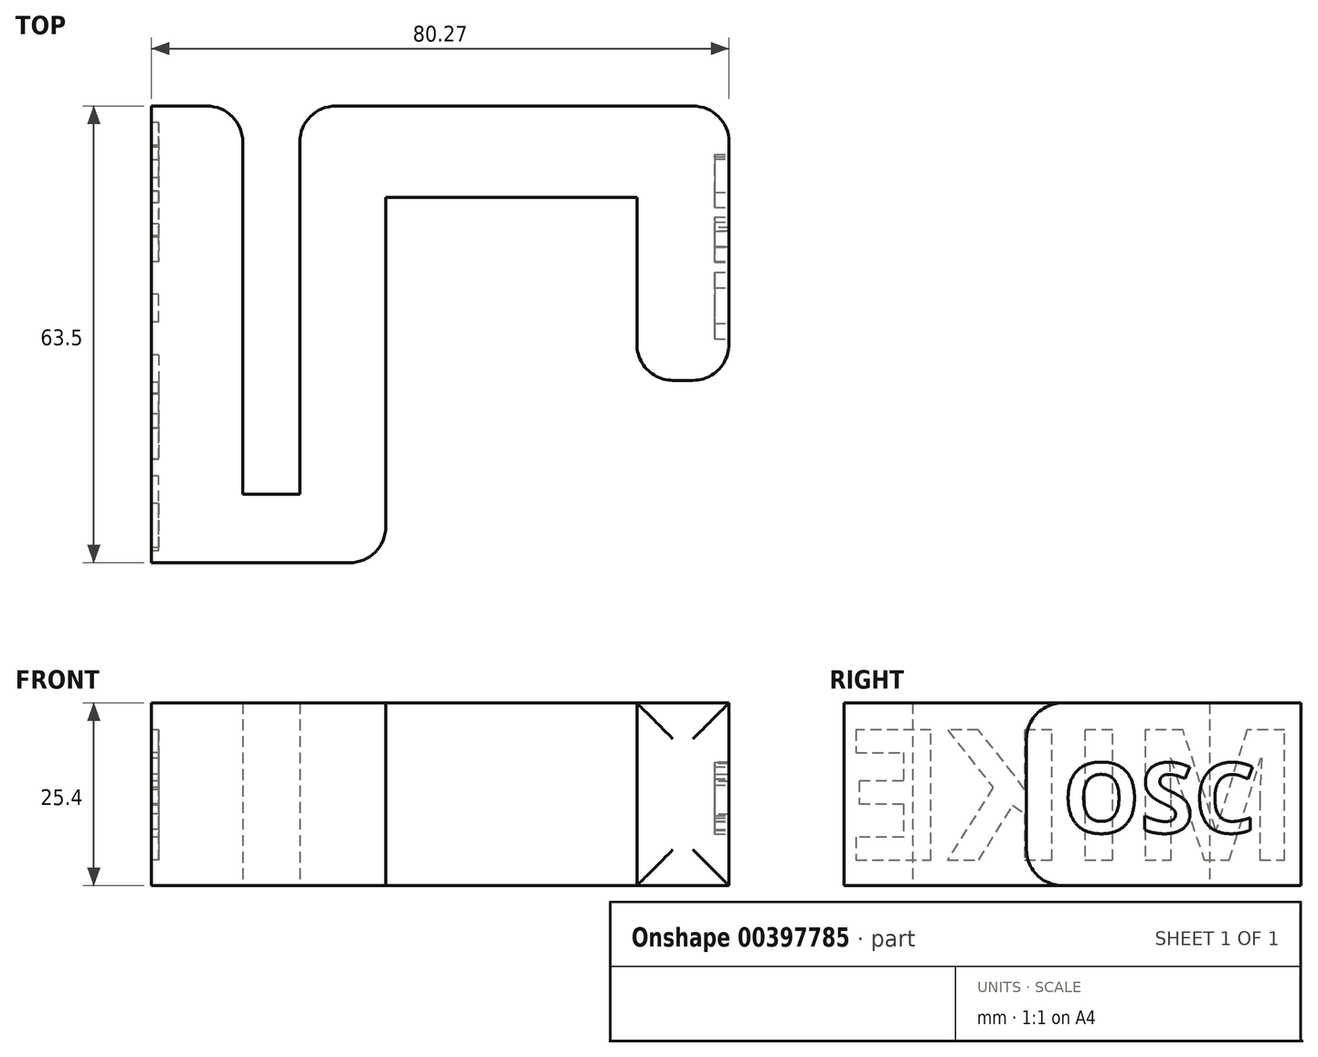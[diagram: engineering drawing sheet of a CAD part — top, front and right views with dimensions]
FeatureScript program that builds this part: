
annotation { "Feature Type Name" : "Feature", "Feature Type Description" : "" }
export const myFeature = defineFeature(function(context is Context, id is Id, definition is map)
    precondition{}
    {
        {
            var Q0;
            Q0=qCreatedBy(makeId("Top.planeOp"),FACE);
            var sketch = newSketch(context, id + "F0", { "sketchPlane" : qUnion([Q0])});
            skLineSegment(sketch, "E0", {"start": v(0, 0) * mm, "end": v(0, 63.5) * mm});
            skLineSegment(sketch, "E1", {"start": v(0, 63.5) * mm, "end": v(12.7, 63.5) * mm});
            skLineSegment(sketch, "E2", {"start": v(12.7, 63.5) * mm, "end": v(12.7, 9.53) * mm});
            skLineSegment(sketch, "E3", {"start": v(12.7, 9.53) * mm, "end": v(20.64, 9.53) * mm});
            skLineSegment(sketch, "E4", {"start": v(20.64, 9.53) * mm, "end": v(20.64, 63.5) * mm});
            skLineSegment(sketch, "E5", {"start": v(20.64, 63.5) * mm, "end": v(80.27, 63.5) * mm});
            skLineSegment(sketch, "E6", {"start": v(80.27, 63.5) * mm, "end": v(80.27, 25.35) * mm});
            skLineSegment(sketch, "E7", {"start": v(80.27, 25.35) * mm, "end": v(67.48, 25.35) * mm});
            skLineSegment(sketch, "E8", {"start": v(67.48, 25.35) * mm, "end": v(67.48, 50.8) * mm});
            skLineSegment(sketch, "E9", {"start": v(67.48, 50.8) * mm, "end": v(32.58, 50.8) * mm});
            skLineSegment(sketch, "E10", {"start": v(32.58, 50.8) * mm, "end": v(32.58, 0) * mm});
            skLineSegment(sketch, "E11", {"start": v(32.58, 0) * mm, "end": v(0, 0) * mm});
            skSolve(sketch);
        }
        {
            var Q0;
            Q0=makeQuery(id+"F0.imprint","IMPRINT",FACE,{"disambiguationData":[TD([[makeQuery(id+"F0.imprint","IMPRINT",EDGE,{"derivedFrom":sQuery(id+"F0.wireOp",EDGE,"E0")}),-1.0]])]});
            extrude(context, id + "F1", {"entities" : qUnion([Q0]), "depth" : 25.4 * mm});
        }
        {
            var Q0;
            Q0=makeQuery(id+"F1.opExtrude","SWEPT_FACE",FACE,{"disambiguationData":[OSD([sQuery(id+"F0.wireOp",EDGE,"E0")])]});
            var sketch = newSketch(context, id + "F2", { "sketchPlane" : qUnion([Q0])});
            skText(sketch, "E12", { "text": "MIKE", "fontName": "OpenSans-Bold.ttf"});
            const initialGuessF2  = {"E12": [-0.0635, 0.00354, 1, 0, 0.01826]};
            skSetInitialGuess(sketch, initialGuessF2);
            skSolve(sketch);
        }
        {
            var Q0;
            Q0=qSketchRegion(id+"F2",true);
            extrude(context, id + "F3", {"entities" : qUnion([Q0]), "operationType" : NewBodyOperationType.REMOVE, "oppositeDirection" : true, "depth" : 1 * mm});
        }
        {
            var Q0;
            Q0=makeQuery(id+"F1.opExtrude","CAP_EDGE",EDGE,{"disambiguationData":[OSD([sQuery(id+"F0.wireOp",EDGE,"E7")])],"isStart":false});
            var Q1;
            Q1=makeQuery(id+"F1.opExtrude","CAP_EDGE",EDGE,{"disambiguationData":[OSD([sQuery(id+"F0.wireOp",EDGE,"E7")])],"isStart":true});
            var Q2;
            Q2=makeQuery(id+"F1.opExtrude","SWEPT_EDGE",EDGE,{"disambiguationData":[OSD([sQuery(id+"F0.wireOp",EDGE,"E6"),sQuery(id+"F0.wireOp",EDGE,"E7")])]});
            var Q3;
            Q3=makeQuery(id+"F1.opExtrude","SWEPT_EDGE",EDGE,{"disambiguationData":[OSD([sQuery(id+"F0.wireOp",EDGE,"E7"),sQuery(id+"F0.wireOp",EDGE,"E8")])]});
            var Q4;
            Q4=makeQuery(id+"F1.opExtrude","SWEPT_EDGE",EDGE,{"disambiguationData":[OSD([sQuery(id+"F0.wireOp",EDGE,"E5"),sQuery(id+"F0.wireOp",EDGE,"E6")])]});
            var Q5;
            Q5=makeQuery(id+"F1.opExtrude","SWEPT_EDGE",EDGE,{"disambiguationData":[OSD([sQuery(id+"F0.wireOp",EDGE,"E10"),sQuery(id+"F0.wireOp",EDGE,"E11")])]});
            var Q6;
            Q6=makeQuery(id+"F1.opExtrude","SWEPT_EDGE",EDGE,{"disambiguationData":[OSD([sQuery(id+"F0.wireOp",EDGE,"E4"),sQuery(id+"F0.wireOp",EDGE,"E5")])]});
            var Q7;
            Q7=makeQuery(id+"F1.opExtrude","SWEPT_EDGE",EDGE,{"disambiguationData":[OSD([sQuery(id+"F0.wireOp",EDGE,"E1"),sQuery(id+"F0.wireOp",EDGE,"E2")])]});
            fillet(context, id + "F4", {"entities" : qUnion([Q0, Q1, Q2, Q3, Q4, Q5, Q6, Q7]), "radius" : 5 * mm, "tangentPropagation" : true, "allowEdgeOverflow" : false});
        }
        {
            var Q0;
            Q0=makeQuery(id+"F1.opExtrude","SWEPT_FACE",FACE,{"disambiguationData":[OSD([sQuery(id+"F0.wireOp",EDGE,"E6")])]});
            var sketch = newSketch(context, id + "F5", { "sketchPlane" : qUnion([Q0])});
            skText(sketch, "E13", { "text": "OSC", "fontName": "OpenSans-Bold.ttf"});
            const initialGuessF5  = {"E13": [0.03035, 0.00734, 1, 0, 0.00977]};
            skSetInitialGuess(sketch, initialGuessF5);
            skSolve(sketch);
        }
        {
            var Q0;
            Q0 = qSketchRegion(id + "F5", true);
            extrude(context, id + "F6", {"entities" : qUnion([Q0]), "operationType" : NewBodyOperationType.REMOVE, "oppositeDirection" : true, "depth" : 2 * mm, "offsetDistance" : 25 * mm});
        }
    });
